# Revit family: Window_Sliding_Flush_Ready-Access_131
name_source: partatom
category: Windows
units: mm (PartAtom-declared; Revit-internal decimal feet)

## family parameters
Always vertical = Yes
Classification Number = 23.30.20.24.14
Cut with Voids When Loaded = No
Host = Wall
Room Calculation Point = No
Shared = No

## types (8) — shared parameters
Air Infiltration = as Specified
Assembly Code = B2020100
Construction Details = http://www.arcat.com
Fixed Window Width = 1' - 2 1/2"
Forced Entry Rating = as Specified
Frame Thickness = 0' - 4"
Keynote = 08582
Manufacturer = Ready Access
Manufacturer Fax = 630-876-7767
Manufacturer Website = http://www.ready-access.com
Meets Egress = as Specified
Miami Dade Conformance = as Specified
Product Data = http://www.arcat.com
Sales Information = http://www.ready-access.com
Send Message = http://www.arcat.com
Service Opening Width = 1' - 6"
Specification = http://www.arcat.com
Standards Conformance = as Specified
Structural Test Pressure = as Specified
URL = http://www.ready-access.com
Wall Closure = By host
Water Penetration = as Specified
Width = 4' - 5 1/2"
zero-valued in all types: Expected Lifespan (Years), Maintenance Schedule (Months), Sound Transmission Class (STC), Warranty Duration (Years)

## per-type parameters (varying)
| type | Description | Electrical_Amperage | Electrical_Frequency | Electrical_Voltage | Height | Model | Service Opening Height |
| Automatic International 18x37 Serving Area | Ready Access Automatic Bi-Parting Sliding Service Window - 131-6E as Specified | 8 A | 60 Hz | 220 V | 3' - 7 3/4" | 131-6E | 3' - 1" |
| Automatic International 18x31 Serving Area | Ready Access Automatic Bi-Parting Sliding Service Window - 131E as Specified | 8 A | 60 Hz | 220 V | 3' - 1 3/4" | 131E | 2' - 7" |
| Automatic Domestic 18x37 Serving Area | Ready Access Automatic Bi-Parting Sliding Service Window - 131-6E as Specified | 15 A | 60 Hz | 115 V | 3' - 7 3/4" | 131-6E | 3' - 1" |
| Automatic Domestic 18x31 Serving Area | Ready Access Automatic Bi-Parting Sliding Service Window - 131E as Specified | 15 A | 60 Hz | 115 V | 3' - 1 3/4" | 131E | 2' - 7" |
| Manual Self Closing 18x37 Serving Area | Ready Access Manual Self Closing Bi-Parting Sliding Service Window - 131-6Sc as Specified | 0 A | 0 Hz | 0 V | 3' - 7 3/4" | 131-6SC | 3' - 1" |
| Manual Self Closing 18x31 Serving Area | Ready Access Manual Self Closing Bi-Parting Sliding Service Window - 131SC as Specified | 0 A | 0 Hz | 0 V | 3' - 1 3/4" | 131SC | 2' - 7" |
| Manual 18x37 Serving Area | Ready Access Manual Bi-Parting Sliding Service Window - 131-6M as Specified | 0 A | 0 Hz | 0 V | 3' - 7 3/4" | 131-6M | 3' - 1" |
| Manual 18x31 Serving Area | Ready Access Manual Bi-Parting Sliding Service Window - 131M as Specified | 0 A | 0 Hz | 0 V | 3' - 1 3/4" | 131M | 2' - 7" |

## geometry (parser evidence)
native form markers: Sweep x3
no freeform markers — native parametric forms only
